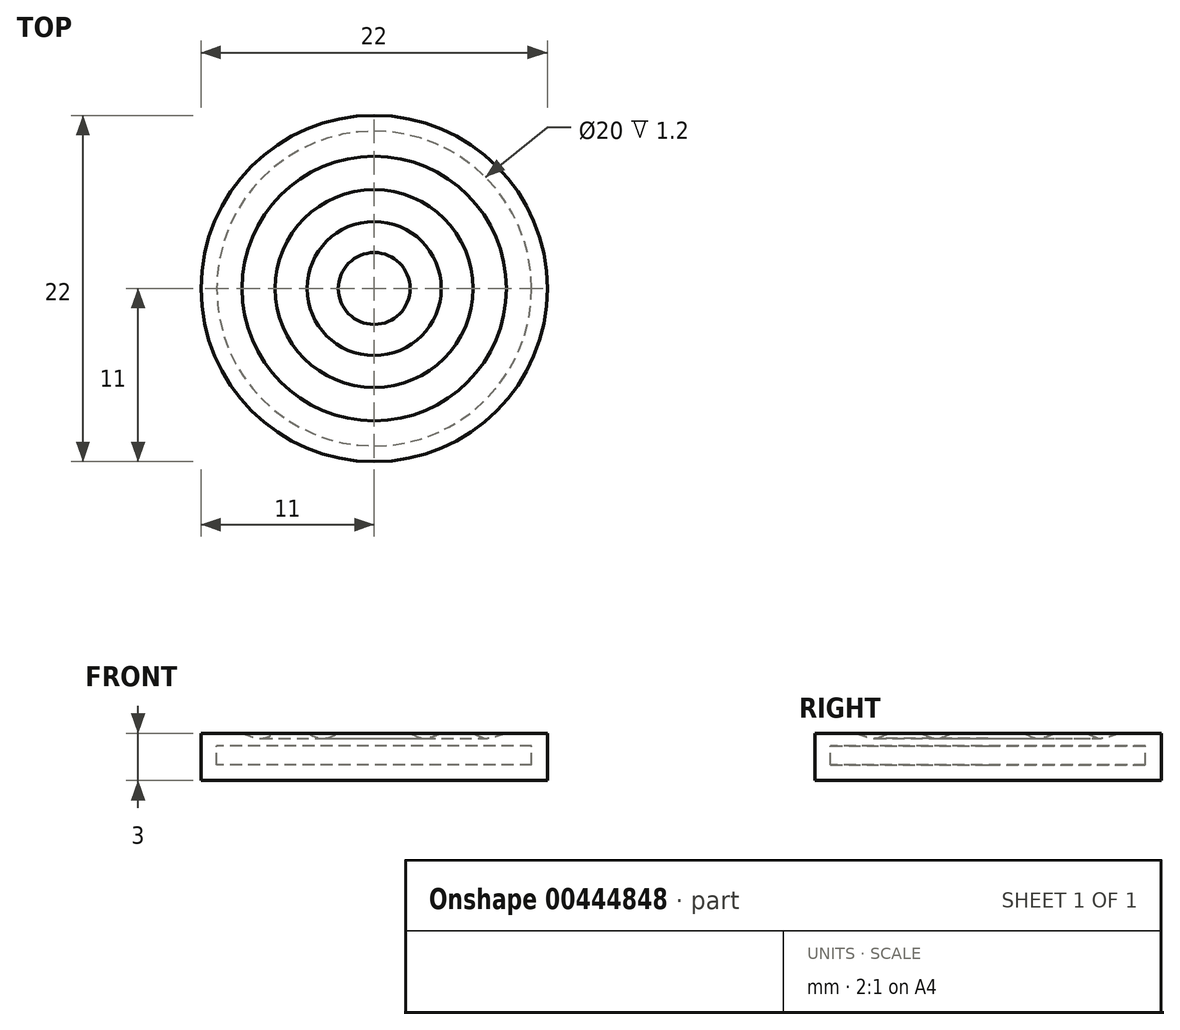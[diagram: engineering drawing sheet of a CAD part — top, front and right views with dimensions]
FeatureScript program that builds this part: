
annotation { "Feature Type Name" : "Feature", "Feature Type Description" : "" }
export const myFeature = defineFeature(function(context is Context, id is Id, definition is map)
    precondition{}
    {
        {
            var Q0;
            Q0=qCreatedBy(makeId("Top.planeOp"),FACE);
            var sketch = newSketch(context, id + "F0", { "sketchPlane" : qUnion([Q0])});
            skCircle(sketch, "E0", {"center": v(0, 0) * mm, "radius": 11 * mm});
            skSolve(sketch);
        }
        {
            var Q0;
            Q0 = qSketchRegion(id + "F0", true);
            extrude(context, id + "F1", {"entities" : qUnion([Q0]), "depth" : 3 * mm});
        }
        {
            var Q0;
            Q0=makeQuery(id+"F1.opExtrude","CAP_FACE",FACE,{"disambiguationData":[OSD([sQuery(id+"F0.wireOp",EDGE,"E0")])],"isStart":false});
            var sketch = newSketch(context, id + "F2", { "sketchPlane" : qUnion([Q0])});
            skCircle(sketch, "E1", {"center": v(0, 0) * mm, "radius": 10 * mm});
            skSolve(sketch);
        }
        {
            var Q0;
            Q0 = qSketchRegion(id + "F2", true);
            extrude(context, id + "F3", {"entities" : qUnion([Q0]), "operationType" : NewBodyOperationType.REMOVE, "oppositeDirection" : true, "depth" : 2 * mm});
        }
        {
            var Q0;
            Q0=qCreatedBy(makeId("Front.planeOp"),FACE);
            var sketch = newSketch(context, id + "F4", { "sketchPlane" : qUnion([Q0])});
            skLineSegment(sketch, "E2.0", {"start": v(-11, 3) * mm, "end": v(11, 3) * mm});
            skLineSegment(sketch, "E3.0", {"start": v(-10, 3) * mm, "end": v(10, 3) * mm});
            skLineSegment(sketch, "E4", {"start": v(-10, 3) * mm, "end": v(-10, 2.2) * mm});
            skLineSegment(sketch, "E5", {"start": v(-10, 2.2) * mm, "end": v(0, 2.2) * mm});
            skLineSegment(sketch, "E6", {"start": v(0, 2.2) * mm, "end": v(0, 4) * mm});
            skPoint(sketch, "E6.endSnap0", {"position": v(0, 3) * mm});
            skFitSpline(sketch, "E7", {"points": [v(-10, 3) * mm, v(-8.4, 3) * mm, v(-7, 2.7) * mm, v(-5.3, 3.33) * mm, v(-3.25, 2.69) * mm, v(-1.4, 3.6) * mm, v(0, 4) * mm], "startDerivative": vector(8.2, 3.65) * mm, "endDerivative": vector(12.92, -0.29) * mm});
            skSolve(sketch);
        }
        {
            var Q0;
            {var subQ7=sQuery(id+"F4.wireOp",EDGE,"E4");Q0=makeQuery(id+"F4.imprint","IMPRINT",FACE,{"disambiguationData":[TD([[makeQuery(id+"F4.imprint","IMPRINT",EDGE,{"derivedFrom":subQ7}),1.0]])]});}
            var Q1;
            {var subQ0=sQuery(id+"F4.wireOp",EDGE,"E7");var subQ1=sQuery(id+"F4.wireOp",EDGE,"E3.0");var subQ2=makeQuery(id+"F4.imprint","INTERSECT",VERTEX,{"disambiguationData":[OD(1.0)],"derivedFrom":[subQ1,subQ0]});Q1=makeQuery(id+"F4.imprint","IMPRINT",FACE,{"disambiguationData":[TD([[makeQuery(id+"F4.imprint","IMPRINT",EDGE,{"disambiguationData":[TD([[subQ2,-1.0]])],"derivedFrom":subQ1}),1.0]])]});}
            var Q2;
            {var subQ0=sQuery(id+"F4.wireOp",EDGE,"E7");var subQ1=sQuery(id+"F4.wireOp",EDGE,"E3.0");var subQ3=makeQuery(id+"F4.imprint","INTERSECT",VERTEX,{"disambiguationData":[OD(0.0)],"derivedFrom":[subQ1,subQ0]});Q2=makeQuery(id+"F4.imprint","IMPRINT",FACE,{"disambiguationData":[TD([[makeQuery(id+"F4.imprint","IMPRINT",EDGE,{"disambiguationData":[TD([[subQ3,1.0]])],"derivedFrom":subQ1}),1.0]])]});}
            var Q3;
            {var subQ0=sQuery(id+"F4.wireOp",EDGE,"E6");var subQ1=sQuery(id+"F4.wireOp",EDGE,"E3.0");var subQ2=makeQuery(id+"F4.imprint","INTERSECT",VERTEX,{"derivedFrom":[subQ1,subQ0]});Q3=makeQuery(id+"F4.imprint","IMPRINT",FACE,{"disambiguationData":[TD([[makeQuery(id+"F4.imprint","IMPRINT",EDGE,{"disambiguationData":[TD([[subQ2,1.0]])],"derivedFrom":subQ1}),1.0]])]});}
            var Q4;
            Q4=sQuery(id+"F4.wireOp",EDGE,"E6");
            revolve(context, id + "F5", {"operationType" : NewBodyOperationType.ADD, "entities" : qUnion([Q0, Q1, Q2, Q3]), "axis" : qUnion([Q4]), "revolveType" : RevolveType.FULL});
        }
    });
